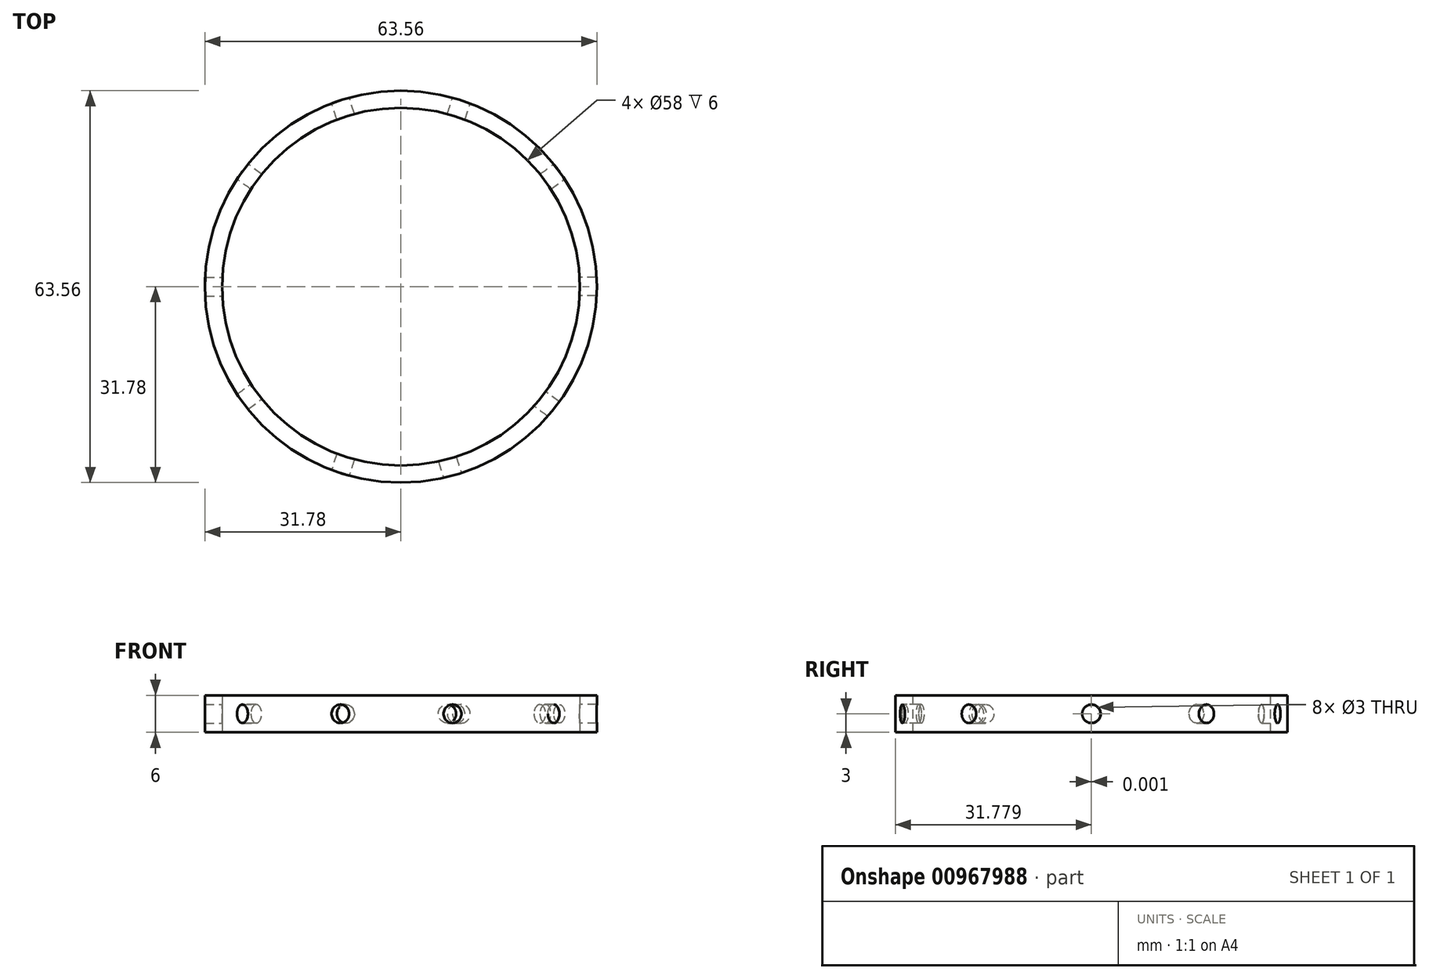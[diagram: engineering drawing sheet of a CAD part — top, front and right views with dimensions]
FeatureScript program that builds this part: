
annotation { "Feature Type Name" : "Feature", "Feature Type Description" : "" }
export const myFeature = defineFeature(function(context is Context, id is Id, definition is map)
    precondition{}
    {
        {
            var Q0;
            Q0=qCreatedBy(makeId("Top.planeOp"),FACE);
            var sketch = newSketch(context, id + "F0", { "sketchPlane" : qUnion([Q0])});
            skCircle(sketch, "E0.cCircle", {"center": v(0, 0) * mm, "radius": 35 * mm, "construction": true});
            skLineSegment(sketch, "E0.0", {"start": v(33.29, 10.82) * mm, "end": v(33.29, -10.82) * mm});
            skLineSegment(sketch, "E0.1", {"start": v(33.29, -10.82) * mm, "end": v(20.57, -28.32) * mm});
            skLineSegment(sketch, "E0.2", {"start": v(20.57, -28.32) * mm, "end": v(0, -35) * mm});
            skLineSegment(sketch, "E0.3", {"start": v(0, -35) * mm, "end": v(-20.57, -28.32) * mm});
            skLineSegment(sketch, "E0.4", {"start": v(-20.57, -28.32) * mm, "end": v(-33.29, -10.82) * mm});
            skLineSegment(sketch, "E0.5", {"start": v(-33.29, -10.82) * mm, "end": v(-33.29, 10.82) * mm});
            skLineSegment(sketch, "E0.6", {"start": v(-33.29, 10.82) * mm, "end": v(-20.57, 28.32) * mm});
            skLineSegment(sketch, "E0.7", {"start": v(-20.57, 28.32) * mm, "end": v(0, 35) * mm});
            skLineSegment(sketch, "E0.8", {"start": v(0, 35) * mm, "end": v(20.57, 28.32) * mm});
            skLineSegment(sketch, "E0.9", {"start": v(20.57, 28.32) * mm, "end": v(33.29, 10.82) * mm});
            skCircle(sketch, "E1", {"center": v(0, 0) * mm, "radius": 29 * mm});
            skSolve(sketch);
        }
        {
            var Q0;
            Q0=makeQuery(id+"F0.imprint","IMPRINT",FACE,{"disambiguationData":[TD([[makeQuery(id+"F0.imprint","IMPRINT",EDGE,{"derivedFrom":sQuery(id+"F0.wireOp",EDGE,"E0.0")}),-1.0]])]});
            extrude(context, id + "F1", {"entities" : qUnion([Q0]), "depth" : 6 * mm, "offsetDistance" : 25 * mm});
        }
        {
            var Q0;
            Q0=makeQuery(id+"F1.opExtrude","SWEPT_FACE",FACE,{"disambiguationData":[OSD([sQuery(id+"F0.wireOp",EDGE,"E0.8")])]});
            var sketch = newSketch(context, id + "F2", { "sketchPlane" : qUnion([Q0])});
            skCircle(sketch, "E2", {"center": v(0, 3) * mm, "radius": 1.5 * mm});
            skSolve(sketch);
        }
        {
            var Q0;
            Q0=makeQuery(id+"F1.opExtrude","SWEPT_FACE",FACE,{"disambiguationData":[OSD([sQuery(id+"F0.wireOp",EDGE,"E0.9")])]});
            var sketch = newSketch(context, id + "F3", { "sketchPlane" : qUnion([Q0])});
            skCircle(sketch, "E3", {"center": v(0, 3) * mm, "radius": 1.5 * mm});
            skSolve(sketch);
        }
        {
            var Q0;
            Q0=makeQuery(id+"F1.opExtrude","SWEPT_FACE",FACE,{"disambiguationData":[OSD([sQuery(id+"F0.wireOp",EDGE,"E0.0")])]});
            var sketch = newSketch(context, id + "F4", { "sketchPlane" : qUnion([Q0])});
            skCircle(sketch, "E4", {"center": v(0, 3) * mm, "radius": 1.5 * mm});
            skSolve(sketch);
        }
        {
            var Q0;
            Q0=makeQuery(id+"F1.opExtrude","SWEPT_FACE",FACE,{"disambiguationData":[OSD([sQuery(id+"F0.wireOp",EDGE,"E0.7")])]});
            var sketch = newSketch(context, id + "F5", { "sketchPlane" : qUnion([Q0])});
            skCircle(sketch, "E5", {"center": v(0, 3) * mm, "radius": 1.5 * mm});
            skSolve(sketch);
        }
        {
            var Q0;
            Q0=makeQuery(id+"F1.opExtrude","SWEPT_FACE",FACE,{"disambiguationData":[OSD([sQuery(id+"F0.wireOp",EDGE,"E0.6")])]});
            var sketch = newSketch(context, id + "F6", { "sketchPlane" : qUnion([Q0])});
            skCircle(sketch, "E6", {"center": v(0, 3) * mm, "radius": 1.5 * mm});
            skSolve(sketch);
        }
        {
            var Q0;
            Q0=makeQuery(id+"F1.opExtrude","SWEPT_FACE",FACE,{"disambiguationData":[OSD([sQuery(id+"F0.wireOp",EDGE,"E0.5")])]});
            var sketch = newSketch(context, id + "F7", { "sketchPlane" : qUnion([Q0])});
            skCircle(sketch, "E7", {"center": v(0, 3) * mm, "radius": 1.5 * mm});
            skSolve(sketch);
        }
        {
            var Q0;
            Q0=makeQuery(id+"F1.opExtrude","SWEPT_FACE",FACE,{"disambiguationData":[OSD([sQuery(id+"F0.wireOp",EDGE,"E0.4")])]});
            var sketch = newSketch(context, id + "F8", { "sketchPlane" : qUnion([Q0])});
            skCircle(sketch, "E8", {"center": v(0, 3) * mm, "radius": 1.5 * mm});
            skSolve(sketch);
        }
        {
            var Q0;
            Q0=makeQuery(id+"F1.opExtrude","SWEPT_FACE",FACE,{"disambiguationData":[OSD([sQuery(id+"F0.wireOp",EDGE,"E0.3")])]});
            var sketch = newSketch(context, id + "F9", { "sketchPlane" : qUnion([Q0])});
            skCircle(sketch, "E9", {"center": v(0, 3) * mm, "radius": 1.5 * mm});
            skSolve(sketch);
        }
        {
            var Q0;
            Q0=makeQuery(id+"F1.opExtrude","SWEPT_FACE",FACE,{"disambiguationData":[OSD([sQuery(id+"F0.wireOp",EDGE,"E0.2")])]});
            var sketch = newSketch(context, id + "F10", { "sketchPlane" : qUnion([Q0])});
            skCircle(sketch, "E10", {"center": v(-1.5, 3) * mm, "radius": 1.5 * mm});
            skSolve(sketch);
        }
        {
            var Q0;
            Q0=makeQuery(id+"F1.opExtrude","SWEPT_FACE",FACE,{"disambiguationData":[OSD([sQuery(id+"F0.wireOp",EDGE,"E0.1")])]});
            var sketch = newSketch(context, id + "F11", { "sketchPlane" : qUnion([Q0])});
            skCircle(sketch, "E11", {"center": v(-1.5, 3) * mm, "radius": 1.5 * mm});
            skSolve(sketch);
        }
        {
            var Q0;
            Q0=makeQuery(id+"F9.imprint","IMPRINT",FACE,{"disambiguationData":[TD([[makeQuery(id+"F9.imprint","IMPRINT",EDGE,{"derivedFrom":sQuery(id+"F9.wireOp",EDGE,"E9")}),1.0]])]});
            extrude(context, id + "F12", {"entities" : qUnion([Q0]), "operationType" : NewBodyOperationType.REMOVE, "oppositeDirection" : true, "depth" : 5 * mm, "offsetDistance" : 25 * mm, "hasSecondDirection" : true, "secondDirectionOppositeDirection" : false, "secondDirectionDepth" : 10 * mm});
        }
        {
            var Q0;
            Q0=makeQuery(id+"F10.imprint","IMPRINT",FACE,{"disambiguationData":[TD([[makeQuery(id+"F10.imprint","IMPRINT",EDGE,{"derivedFrom":sQuery(id+"F10.wireOp",EDGE,"E10")}),1.0]])]});
            var Q1;
            Q1=sQuery(id+"F10.wireOp",EDGE,"E10");
            extrude(context, id + "F13", {"entities" : qUnion([Q0]), "operationType" : NewBodyOperationType.REMOVE, "surfaceEntities" : qUnion([Q1]), "oppositeDirection" : true, "depth" : 5 * mm, "offsetDistance" : 25 * mm, "hasSecondDirection" : true, "secondDirectionOppositeDirection" : false, "secondDirectionDepth" : 10 * mm});
        }
        {
            var Q0;
            Q0=makeQuery(id+"F8.imprint","IMPRINT",FACE,{"disambiguationData":[TD([[makeQuery(id+"F8.imprint","IMPRINT",EDGE,{"derivedFrom":sQuery(id+"F8.wireOp",EDGE,"E8")}),1.0]])]});
            extrude(context, id + "F14", {"entities" : qUnion([Q0]), "operationType" : NewBodyOperationType.REMOVE, "depth" : 5 * mm, "offsetDistance" : 25 * mm, "hasSecondDirection" : true, "secondDirectionOppositeDirection" : true, "secondDirectionDepth" : 10 * mm});
        }
        {
            var Q0;
            Q0=makeQuery(id+"F11.imprint","IMPRINT",FACE,{"disambiguationData":[TD([[makeQuery(id+"F11.imprint","IMPRINT",EDGE,{"derivedFrom":sQuery(id+"F11.wireOp",EDGE,"E11")}),1.0]])]});
            extrude(context, id + "F15", {"entities" : qUnion([Q0]), "operationType" : NewBodyOperationType.REMOVE, "depth" : 5 * mm, "offsetDistance" : 25 * mm, "hasSecondDirection" : true, "secondDirectionOppositeDirection" : true, "secondDirectionDepth" : 10 * mm});
        }
        {
            var Q0;
            Q0=makeQuery(id+"F4.imprint","IMPRINT",FACE,{"disambiguationData":[TD([[makeQuery(id+"F4.imprint","IMPRINT",EDGE,{"derivedFrom":sQuery(id+"F4.wireOp",EDGE,"E4")}),1.0]])]});
            extrude(context, id + "F16", {"entities" : qUnion([Q0]), "operationType" : NewBodyOperationType.REMOVE, "depth" : 5 * mm, "offsetDistance" : 25 * mm, "hasSecondDirection" : true, "secondDirectionOppositeDirection" : true, "secondDirectionDepth" : 10 * mm});
        }
        {
            var Q0;
            Q0=makeQuery(id+"F7.imprint","IMPRINT",FACE,{"disambiguationData":[TD([[makeQuery(id+"F7.imprint","IMPRINT",EDGE,{"derivedFrom":sQuery(id+"F7.wireOp",EDGE,"E7")}),1.0]])]});
            extrude(context, id + "F17", {"entities" : qUnion([Q0]), "operationType" : NewBodyOperationType.REMOVE, "depth" : 5 * mm, "offsetDistance" : 25 * mm, "hasSecondDirection" : true, "secondDirectionOppositeDirection" : true, "secondDirectionDepth" : 10 * mm});
        }
        {
            var Q0;
            Q0=makeQuery(id+"F6.imprint","IMPRINT",FACE,{"disambiguationData":[TD([[makeQuery(id+"F6.imprint","IMPRINT",EDGE,{"derivedFrom":sQuery(id+"F6.wireOp",EDGE,"E6")}),1.0]])]});
            extrude(context, id + "F18", {"entities" : qUnion([Q0]), "operationType" : NewBodyOperationType.REMOVE, "oppositeDirection" : true, "depth" : 5 * mm, "offsetDistance" : 25 * mm, "hasSecondDirection" : true, "secondDirectionOppositeDirection" : false, "secondDirectionDepth" : 10 * mm});
        }
        {
            var Q0;
            Q0=makeQuery(id+"F5.imprint","IMPRINT",FACE,{"disambiguationData":[TD([[makeQuery(id+"F5.imprint","IMPRINT",EDGE,{"derivedFrom":sQuery(id+"F5.wireOp",EDGE,"E5")}),1.0]])]});
            extrude(context, id + "F19", {"entities" : qUnion([Q0]), "operationType" : NewBodyOperationType.REMOVE, "oppositeDirection" : true, "depth" : 5 * mm, "offsetDistance" : 25 * mm, "hasSecondDirection" : true, "secondDirectionOppositeDirection" : false, "secondDirectionDepth" : 10 * mm});
        }
        {
            var Q0;
            Q0=makeQuery(id+"F3.imprint","IMPRINT",FACE,{"disambiguationData":[TD([[makeQuery(id+"F3.imprint","IMPRINT",EDGE,{"derivedFrom":sQuery(id+"F3.wireOp",EDGE,"E3")}),1.0]])]});
            extrude(context, id + "F20", {"entities" : qUnion([Q0]), "operationType" : NewBodyOperationType.REMOVE, "oppositeDirection" : true, "depth" : 5 * mm, "offsetDistance" : 25 * mm, "hasSecondDirection" : true, "secondDirectionOppositeDirection" : false, "secondDirectionDepth" : 10 * mm});
        }
        {
            var Q0;
            Q0=qCreatedBy(makeId("Top.planeOp"),FACE);
            var sketch = newSketch(context, id + "F21", { "sketchPlane" : qUnion([Q0])});
            skCircle(sketch, "E12", {"center": v(0, 0) * mm, "radius": 31.77 * mm});
            skCircle(sketch, "E13", {"center": v(0, 0) * mm, "radius": 36.5 * mm});
            skSolve(sketch);
        }
        {
            var Q0;
            Q0 = qSketchRegion(id + "F21", true);
            extrude(context, id + "F22", {"entities" : qUnion([Q0]), "operationType" : NewBodyOperationType.REMOVE, "depth" : 6 * mm, "offsetDistance" : 25 * mm});
        }
        {
            var Q0;
            Q0=makeQuery(id+"F2.imprint","IMPRINT",FACE,{"disambiguationData":[TD([[makeQuery(id+"F2.imprint","IMPRINT",EDGE,{"derivedFrom":sQuery(id+"F2.wireOp",EDGE,"E2")}),1.0]])]});
            extrude(context, id + "F23", {"entities" : qUnion([Q0]), "operationType" : NewBodyOperationType.REMOVE, "oppositeDirection" : true, "depth" : 10 * mm, "offsetDistance" : 25 * mm});
        }
    });
